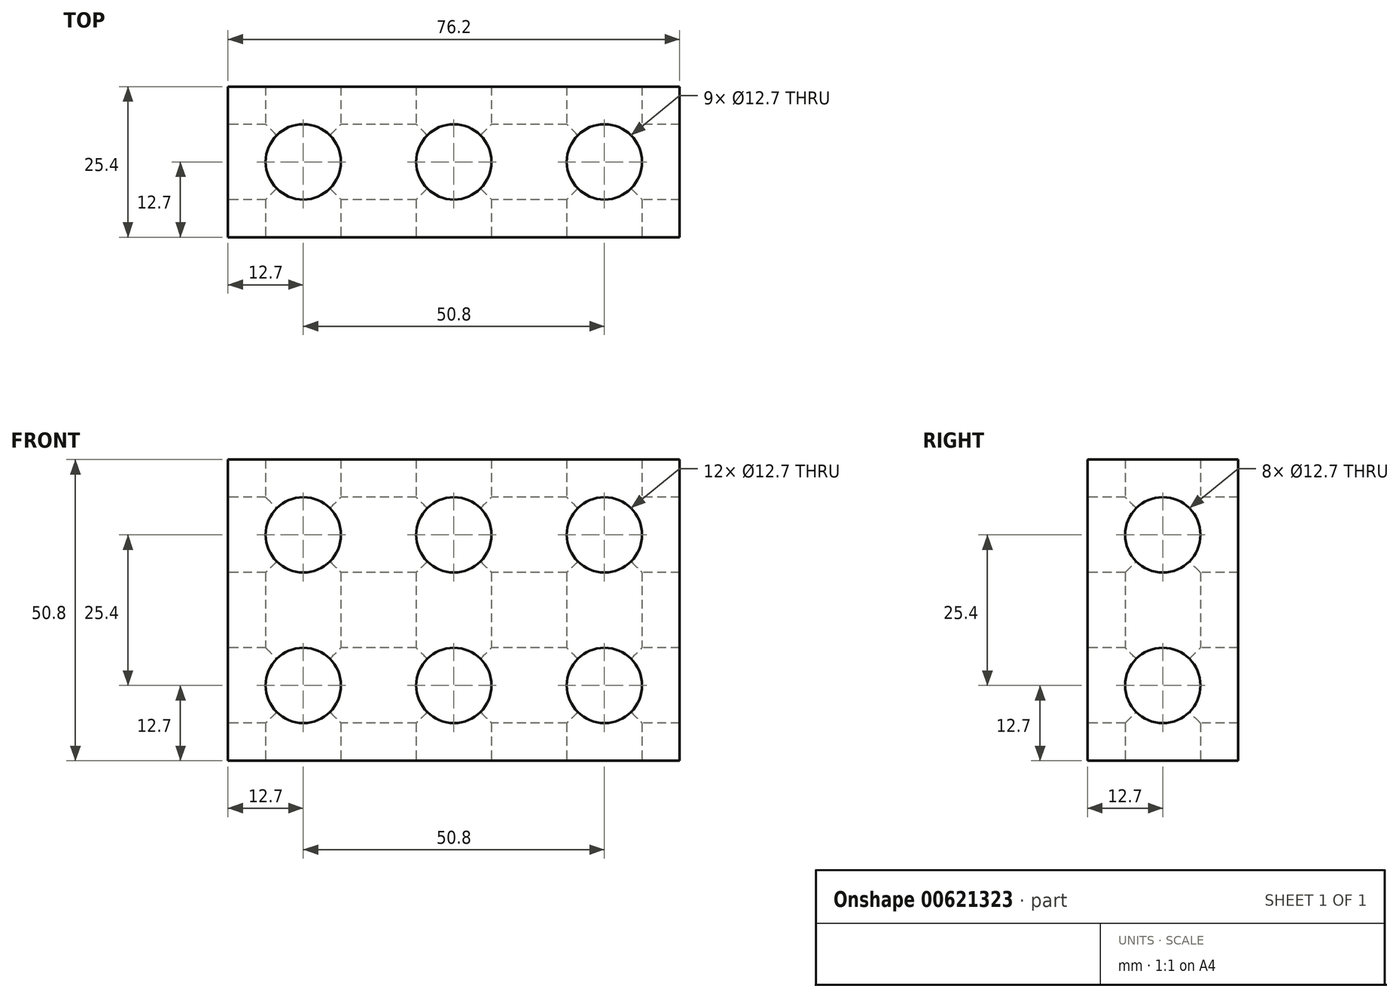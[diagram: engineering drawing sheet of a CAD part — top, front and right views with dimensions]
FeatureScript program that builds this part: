
annotation { "Feature Type Name" : "Feature", "Feature Type Description" : "" }
export const myFeature = defineFeature(function(context is Context, id is Id, definition is map)
    precondition{}
    {
        {
            var Q0;
            Q0=qCreatedBy(makeId("Front.planeOp"),FACE);
            var sketch = newSketch(context, id + "F0", { "sketchPlane" : qUnion([Q0])});
            skLineSegment(sketch, "E0.bottom", {"start": v(38.1, -25.4) * mm, "end": v(-38.1, -25.4) * mm});
            skLineSegment(sketch, "E0.top", {"start": v(38.1, 25.4) * mm, "end": v(-38.1, 25.4) * mm});
            skLineSegment(sketch, "E0.left", {"start": v(38.1, -25.4) * mm, "end": v(38.1, 25.4) * mm});
            skLineSegment(sketch, "E0.right", {"start": v(-38.1, -25.4) * mm, "end": v(-38.1, 25.4) * mm});
            skPoint(sketch, "E0.middle", {"position": v(0, 0) * mm});
            skSolve(sketch);
        }
        {
            var Q0;
            Q0 = qSketchRegion(id + "F0", true);
            extrude(context, id + "F1", {"entities" : qUnion([Q0]), "endBound" : BoundingType.SYMMETRIC, "depth" : 25.4 * mm, "offsetDistance" : 25.4 * mm});
        }
        {
            var Q0;
            Q0=makeQuery(id+"F1.opExtrude","CAP_FACE",FACE,{"disambiguationData":[OSD([sQuery(id+"F0.wireOp",EDGE,"E0.bottom"),sQuery(id+"F0.wireOp",EDGE,"E0.top"),sQuery(id+"F0.wireOp",EDGE,"E0.left"),sQuery(id+"F0.wireOp",EDGE,"E0.right")])],"isStart":false});
            var sketch = newSketch(context, id + "F2", { "sketchPlane" : qUnion([Q0])});
            skCircle(sketch, "E1", {"center": v(-25.4, 12.7) * mm, "radius": 6.35 * mm});
            skCircle(sketch, "E2", {"center": v(0, 12.7) * mm, "radius": 6.35 * mm});
            skCircle(sketch, "E3", {"center": v(25.4, 12.7) * mm, "radius": 6.35 * mm});
            skCircle(sketch, "E4", {"center": v(-25.4, -12.7) * mm, "radius": 6.35 * mm});
            skCircle(sketch, "E5", {"center": v(0, -12.7) * mm, "radius": 6.35 * mm});
            skCircle(sketch, "E6", {"center": v(25.4, -12.7) * mm, "radius": 6.35 * mm});
            skSolve(sketch);
        }
        {
            var Q0;
            Q0 = qSketchRegion(id + "F2", true);
            extrude(context, id + "F3", {"entities" : qUnion([Q0]), "operationType" : NewBodyOperationType.REMOVE, "endBound" : BoundingType.UP_TO_NEXT, "oppositeDirection" : true, "depth" : 25.4 * mm, "offsetDistance" : 25.4 * mm});
        }
        {
            var Q0;
            Q0=makeQuery(id+"F1.opExtrude","SWEPT_FACE",FACE,{"disambiguationData":[OSD([sQuery(id+"F0.wireOp",EDGE,"E0.right")])]});
            var sketch = newSketch(context, id + "F4", { "sketchPlane" : qUnion([Q0])});
            skCircle(sketch, "E7", {"center": v(0, 12.7) * mm, "radius": 6.35 * mm});
            skCircle(sketch, "E8", {"center": v(0, -12.7) * mm, "radius": 6.35 * mm});
            skSolve(sketch);
        }
        {
            var Q0;
            Q0 = qSketchRegion(id + "F4", true);
            var Q1;
            Q1=makeQuery(id+"F1.opExtrude","SWEPT_FACE",FACE,{"disambiguationData":[OSD([sQuery(id+"F0.wireOp",EDGE,"E0.left")])]});
            extrude(context, id + "F5", {"entities" : qUnion([Q0]), "operationType" : NewBodyOperationType.REMOVE, "endBound" : BoundingType.UP_TO_SURFACE, "oppositeDirection" : true, "depth" : 25.4 * mm, "endBoundEntityFace" : qUnion([Q1]), "offsetDistance" : 25.4 * mm});
        }
        {
            var Q0;
            Q0=makeQuery(id+"F1.opExtrude","SWEPT_FACE",FACE,{"disambiguationData":[OSD([sQuery(id+"F0.wireOp",EDGE,"E0.bottom")])]});
            var sketch = newSketch(context, id + "F6", { "sketchPlane" : qUnion([Q0])});
            skCircle(sketch, "E9", {"center": v(-25.4, 0) * mm, "radius": 6.35 * mm});
            skCircle(sketch, "E10", {"center": v(0, 0) * mm, "radius": 6.35 * mm});
            skCircle(sketch, "E11", {"center": v(25.4, 0) * mm, "radius": 6.35 * mm});
            skSolve(sketch);
        }
        {
            var Q0;
            Q0 = qSketchRegion(id + "F6", true);
            var Q1;
            Q1=makeQuery(id+"F1.opExtrude","SWEPT_FACE",FACE,{"disambiguationData":[OSD([sQuery(id+"F0.wireOp",EDGE,"E0.top")])]});
            extrude(context, id + "F7", {"entities" : qUnion([Q0]), "operationType" : NewBodyOperationType.REMOVE, "endBound" : BoundingType.UP_TO_SURFACE, "oppositeDirection" : true, "depth" : 25.4 * mm, "endBoundEntityFace" : qUnion([Q1]), "offsetDistance" : 25.4 * mm});
        }
    });
